# Revit family: DIVITYP004
name_source: partatom
category: Furniture
units: mm (PartAtom-declared; Revit-internal decimal feet)

## family parameters
Always vertical = Yes
Cut with Voids When Loaded = No
OmniClass Number = 23.40.20.00
OmniClass Title = General Furniture and Specialties
Render Appearance Source = Family Geometry
Room Calculation Point = No
Shared = No
Work Plane-Based = No

## types (1)
- DIVITYP004
    Cost = 45865 $
    Default Elevation = 0 mm  [stored 0 ft]
    Description = 3 x White Duplex Outlet - Line 1, 3 x White Duplex Outlet - Line 2, 3 x White Duplex Outlet - Line 3, 3 x White Duplex Outlet - Line 4 - Dedicated, 2 x 57 in. Electrical Jumper  (Pt 36E & Vt 48), 1 x 18 in. Electrical Jumper  (Panel To Panel), 1 x LH Receptacle Mounted Base Infeed - 72L - 8 Wire, 4 Circuit, 4 x DiVi LINEAR HARD PANEL-PWR-PERM MONO- 50H X 36W, 2 x DiVi LINEAR Hard PANEL -NPWR-PERM MONO- 50H X 36W, 2 x Divi Gallery Panel End Double - 50H x 84W Horz, 2 x Divi Gallery Panel  Spine Dbl - 50H x 84W Horz, 6 x Pedestal - B/B/F - 24D, 6 x TBL, REC, 2MM, 30DX72WX29H, HAL, E SERIES GLD 2 STAGE, 6 x Rectangular - 2mm Edge - 24D x 42W, 3 x Regular Cantilever - Left Hand - 24D, 3 x Regular Cantilever - Right Hand - 24D, 3 x Divi Channel Screen, Panel Top,GL1/4",12hx72w
    Exported From CET Designer = Yes
    Manufacturer = AIS
    Model = E-MW8W4DO1-W
    Show DIVITYP004 = Yes
    VisibilityIndex = 0

note: [stored X ft] marks values corroborated as IEEE doubles in the binary element streams (Revit-internal decimal feet)

## geometry (parser evidence)
native form markers: Sweep x3
no freeform markers — native parametric forms only
